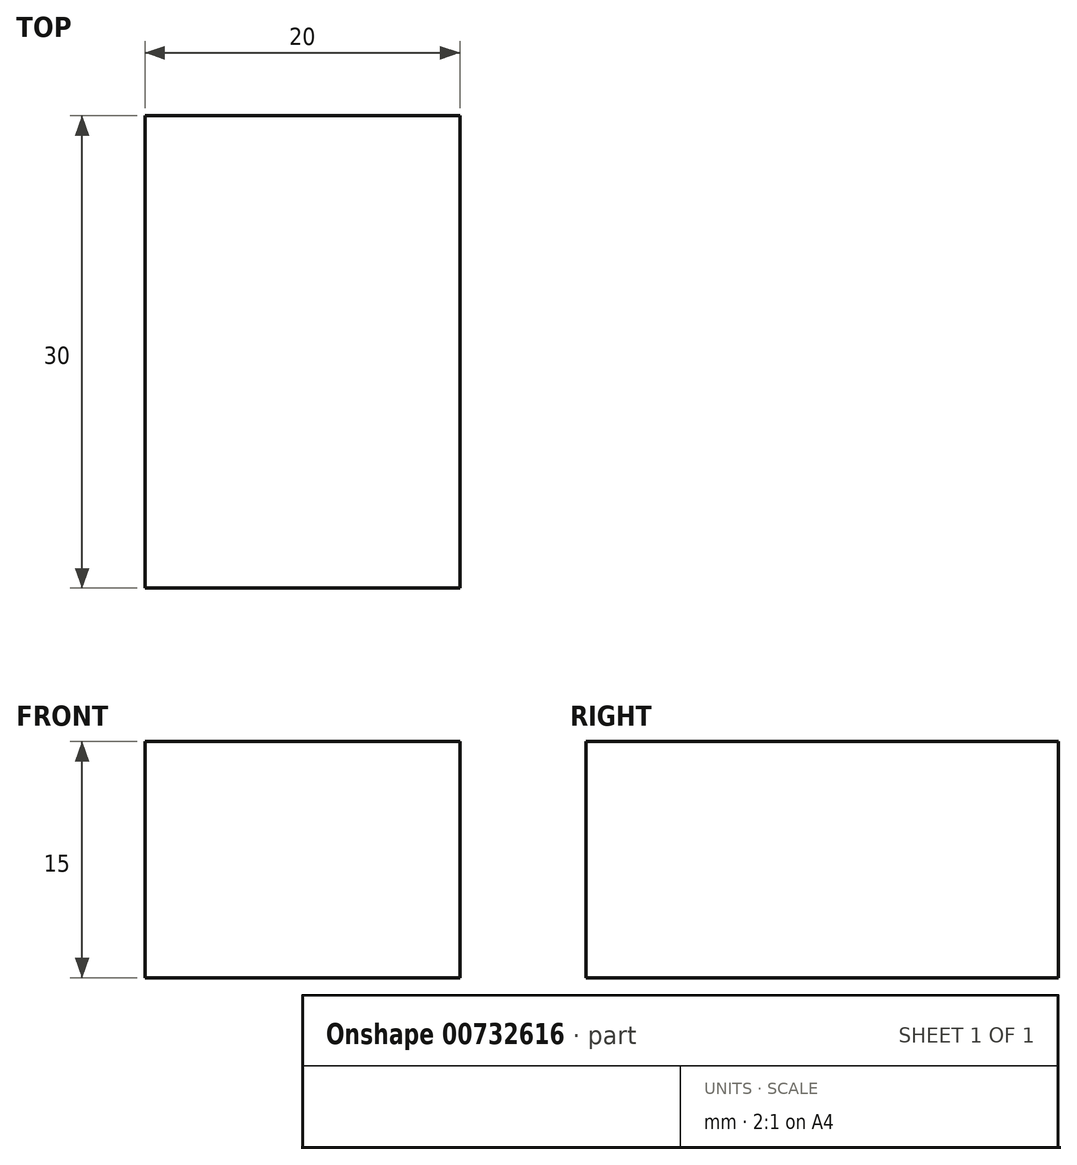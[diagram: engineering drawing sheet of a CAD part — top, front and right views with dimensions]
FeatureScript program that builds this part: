
annotation { "Feature Type Name" : "Feature", "Feature Type Description" : "" }
export const myFeature = defineFeature(function(context is Context, id is Id, definition is map)
    precondition{}
    {
        {
            var Q0;
            Q0=qCreatedBy(makeId("Top.planeOp"),FACE);
            var sketch = newSketch(context, id + "F0", { "sketchPlane" : qUnion([Q0])});
            skLineSegment(sketch, "E0.bottom", {"start": v(-10, 15) * mm, "end": v(10, 15) * mm});
            skLineSegment(sketch, "E0.top", {"start": v(-10, -15) * mm, "end": v(10, -15) * mm});
            skLineSegment(sketch, "E0.left", {"start": v(-10, 15) * mm, "end": v(-10, -15) * mm});
            skLineSegment(sketch, "E0.right", {"start": v(10, 15) * mm, "end": v(10, -15) * mm});
            skPoint(sketch, "E0.middle", {"position": v(0, 0) * mm});
            skSolve(sketch);
        }
        {
            var Q0;
            Q0 = qSketchRegion(id + "F0", true);
            extrude(context, id + "F1", {"entities" : qUnion([Q0]), "depth" : 15 * mm, "offsetDistance" : 25 * mm});
        }
    });
